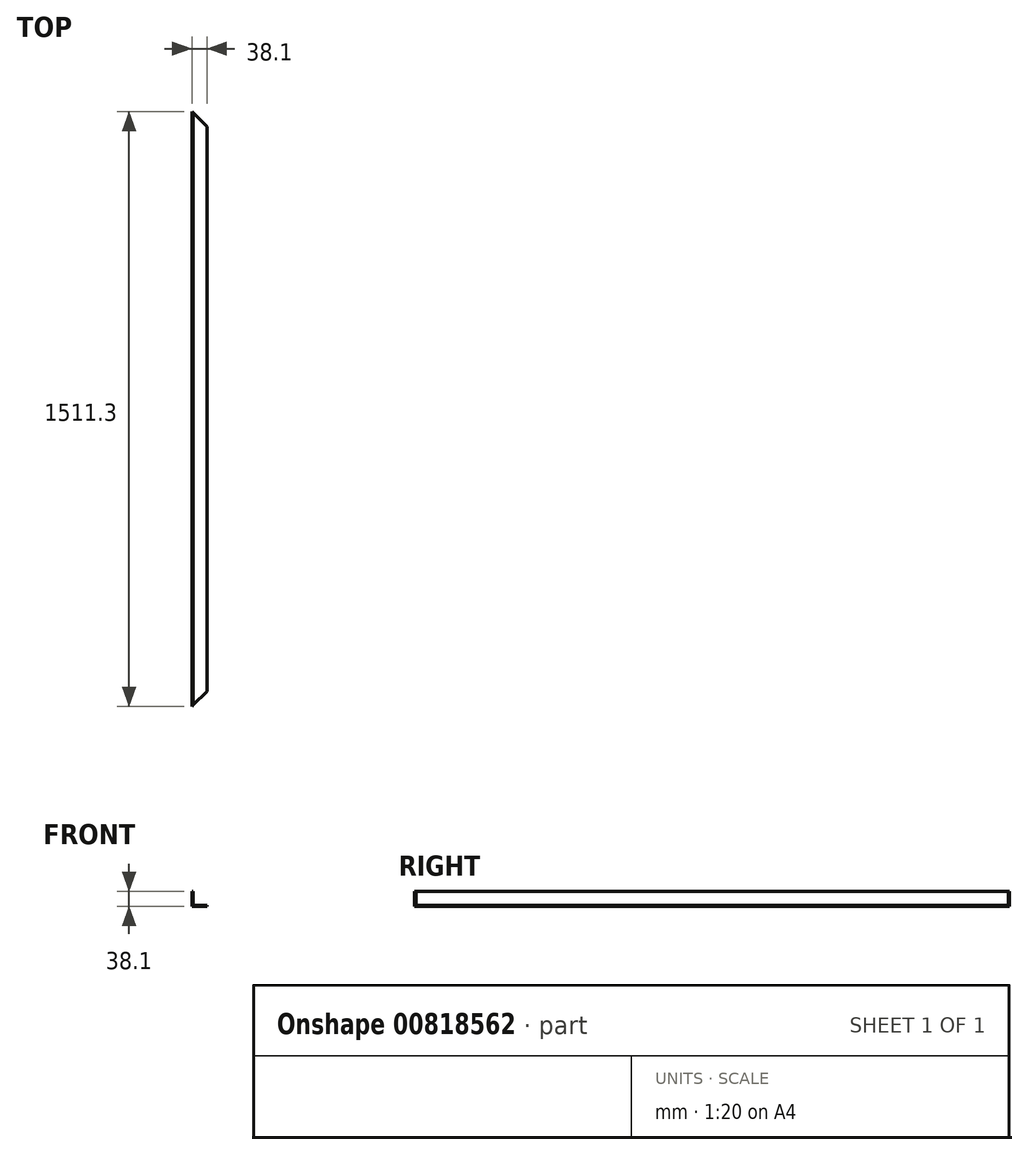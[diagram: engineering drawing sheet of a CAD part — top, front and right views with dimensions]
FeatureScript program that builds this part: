
annotation { "Feature Type Name" : "Feature", "Feature Type Description" : "" }
export const myFeature = defineFeature(function(context is Context, id is Id, definition is map)
    precondition{}
    {
        {
            var Q0;
            Q0=qCreatedBy(makeId("Front.planeOp"),FACE);
            var sketch = newSketch(context, id + "F0", { "sketchPlane" : qUnion([Q0])});
            skLineSegment(sketch, "E0", {"start": v(-21.73, 20.45) * mm, "end": v(-21.73, -17.65) * mm});
            skLineSegment(sketch, "E1", {"start": v(-21.73, -17.65) * mm, "end": v(16.37, -17.65) * mm});
            skLineSegment(sketch, "E2", {"start": v(16.37, -17.65) * mm, "end": v(16.37, -14.47) * mm});
            skLineSegment(sketch, "E3", {"start": v(16.37, -14.47) * mm, "end": v(-18.55, -14.47) * mm});
            skLineSegment(sketch, "E4", {"start": v(-18.55, -14.47) * mm, "end": v(-18.55, 20.45) * mm});
            skLineSegment(sketch, "E5", {"start": v(-18.55, 20.45) * mm, "end": v(-21.73, 20.45) * mm});
            skSolve(sketch);
        }
        {
            var Q0;
            Q0=makeQuery(id+"F0.imprint","IMPRINT",FACE,{"disambiguationData":[TD([[makeQuery(id+"F0.imprint","IMPRINT",EDGE,{"derivedFrom":sQuery(id+"F0.wireOp",EDGE,"E0")}),1.0]])]});
            extrude(context, id + "F1", {"entities" : qUnion([Q0]), "depth" : 1511.3 * mm, "offsetDistance" : 25.4 * mm});
        }
        {
            var Q0;
            Q0=makeQuery(id+"F1.opExtrude","SWEPT_FACE",FACE,{"disambiguationData":[OSD([sQuery(id+"F0.wireOp",EDGE,"E1")])]});
            var sketch = newSketch(context, id + "F2", { "sketchPlane" : qUnion([Q0])});
            skLineSegment(sketch, "E6", {"start": v(-21.73, 1511.3) * mm, "end": v(16.37, 1473.2) * mm});
            skLineSegment(sketch, "E7", {"start": v(16.37, 1473.2) * mm, "end": v(16.37, 1511.3) * mm});
            skLineSegment(sketch, "E8", {"start": v(16.37, 1511.3) * mm, "end": v(-21.73, 1511.3) * mm});
            skLineSegment(sketch, "E9", {"start": v(-21.73, 0) * mm, "end": v(16.37, 38.1) * mm});
            skLineSegment(sketch, "E10", {"start": v(16.37, 38.1) * mm, "end": v(16.37, 0) * mm});
            skLineSegment(sketch, "E11", {"start": v(16.37, 0) * mm, "end": v(-21.73, 0) * mm});
            skSolve(sketch);
        }
        {
            var Q0;
            Q0 = qSketchRegion(id + "F2", true);
            extrude(context, id + "F3", {"entities" : qUnion([Q0]), "operationType" : NewBodyOperationType.REMOVE, "oppositeDirection" : true, "depth" : 38.1 * mm, "offsetDistance" : 25.4 * mm});
        }
    });
